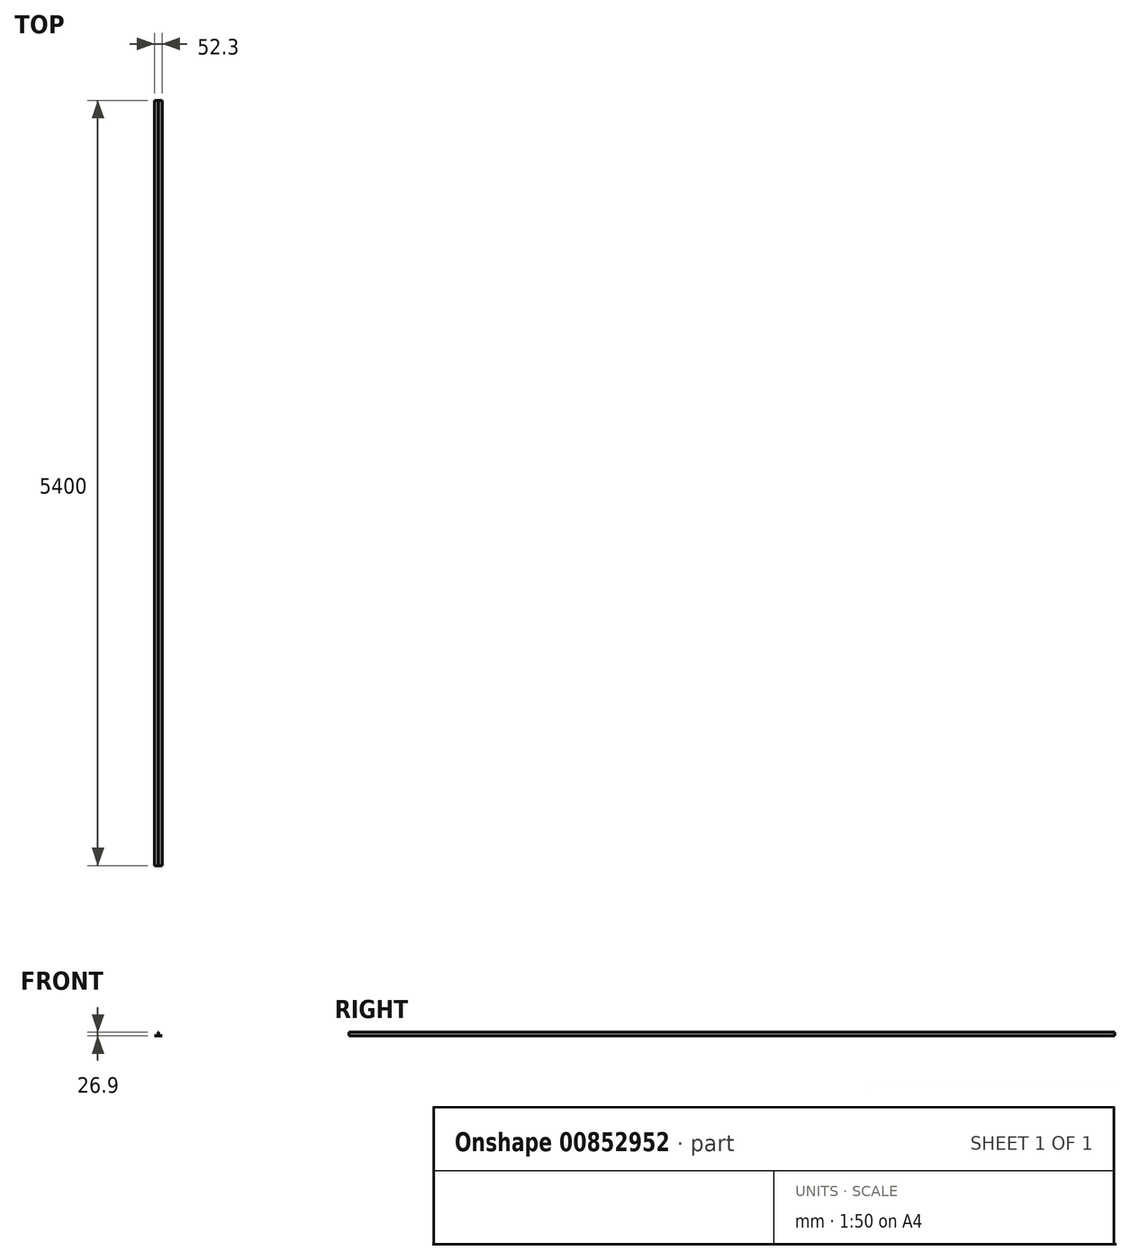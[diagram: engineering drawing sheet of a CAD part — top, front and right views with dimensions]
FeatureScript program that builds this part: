
annotation { "Feature Type Name" : "Feature", "Feature Type Description" : "" }
export const myFeature = defineFeature(function(context is Context, id is Id, definition is map)
    precondition{}
    {
        {
            var Q0;
            Q0=qCreatedBy(makeId("Front.planeOp"),FACE);
            var sketch = newSketch(context, id + "F0", { "sketchPlane" : qUnion([Q0])});
            skLineSegment(sketch, "E0", {"start": v(0, 0) * mm, "end": v(0, 1.5) * mm});
            skLineSegment(sketch, "E1", {"start": v(0, 1.5) * mm, "end": v(25.4, 1.5) * mm});
            skLineSegment(sketch, "E2", {"start": v(25.4, 1.5) * mm, "end": v(25.4, 26.9) * mm});
            skLineSegment(sketch, "E3", {"start": v(25.4, 26.9) * mm, "end": v(26.9, 26.9) * mm});
            skLineSegment(sketch, "E4", {"start": v(26.9, 26.9) * mm, "end": v(26.9, 1.5) * mm});
            skLineSegment(sketch, "E5", {"start": v(26.9, 1.5) * mm, "end": v(52.3, 1.5) * mm});
            skLineSegment(sketch, "E6", {"start": v(52.3, 1.5) * mm, "end": v(52.3, 0) * mm});
            skLineSegment(sketch, "E7", {"start": v(52.3, 0) * mm, "end": v(0, 0) * mm});
            skSolve(sketch);
        }
        {
            var Q0;
            Q0 = qSketchRegion(id + "F0", true);
            extrude(context, id + "F1", {"entities" : qUnion([Q0]), "depth" : 5400 * mm, "offsetDistance" : 25.4 * mm});
        }
    });
